# Revit family: Warp-9
name_source: partatom
category: Lighting Fixtures
revit_build: Autodesk Revit 2013 (Build: 20130531_2115(x64)
units: mm (PartAtom-declared; Revit-internal decimal feet)

## types (2) — shared parameters
Assembly Code = D5020230
Color Filter = 16777215
Description = Large, Electronic LED
Dimming Lamp Color Temperature Shift = <None>
Emit Shape Visible in Rendering = No
Emit from Rectangle Length = 1' - 0"
Emit from Rectangle Width = 1' - 0"
Fixture Height = 0' - 7 1/16"
Glass = Glass
Lamp = LED
Light Case = Aluminum_Kim-Lighting_Black-powder-coat
Load Classification = Lighting
Manufacturer = Kim Lighting
Manufacturer Fax = 626-369-2695
MasterFormat Title = Site Lighting
Model = Wrap 9
Note Visible = Yes
Number of Poles = 1
OmniClass Number = 23.80.70.14.21
OmniClass Title = Streets an Roadway Lighting
Photometric Notes = More IES files download on Photometric Web Link
Photometric Web Link = http://www.kimlighting.com
Pole Finish = Aluminum-KIM-Black
Power Factor = 1
Product Documentation Link = http://www.kimlighting.com
Product Page URL = http://www.kimlighting.com
Revisions Date = 11/07/17
Series = Site/Roadway
URL = http://www.kimlighting.com
Voltage = 277 V
Wattage Comments = 131W to 270W

## per-type parameters (varying)
| type | Apparent Load | Fixture Length | Fixture Mount Height | Fixture Mount Length | Fixture Total  Height | Height | Photometric Web File | Tilt Angle | Watts | Weight | Width |
| WP9L | 175 VA | 2' - 11 1/8" | 0' - 5 27/32" | 0' - 5 1/8" | 0' - 10 5/16" | 0' - 5 1/2" | wp9l2p70-120l5k.ies | 90.00° | 175 W | 0.04 kip | 1' - 8" |
| WP9S | 88 VA | 2' - 2 15/16" | 0' - 5 9/16" | 0' - 4 7/16" | 0' - 8 15/16" | 0' - 4 1/8" | wp9s3p70-60l4k.ies | 60.00° | 88 W | 0.02 kip | 1' - 3" |

## geometry (parser evidence)
native form markers: Blend x20, Sweep x4
no freeform markers — native parametric forms only
